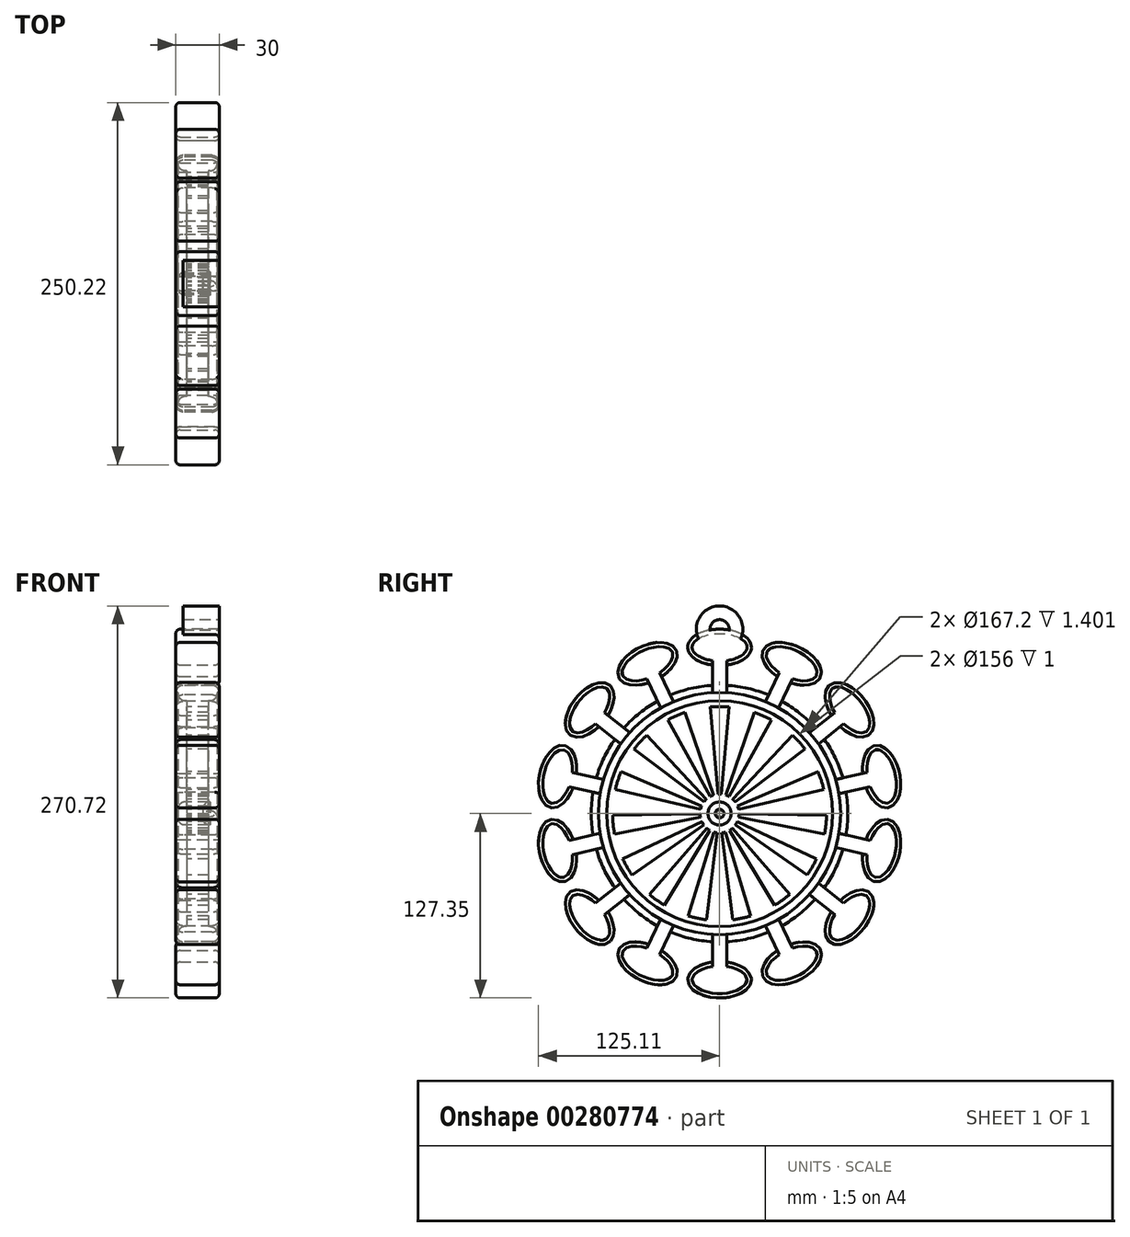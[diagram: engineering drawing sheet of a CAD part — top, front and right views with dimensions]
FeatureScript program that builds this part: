
annotation { "Feature Type Name" : "Feature", "Feature Type Description" : "" }
export const myFeature = defineFeature(function(context is Context, id is Id, definition is map)
    precondition{}
    {
        {
            var Q0;
            Q0=qCreatedBy(makeId("Front.planeOp"),FACE);
            var sketch = newSketch(context, id + "F0", { "sketchPlane" : qUnion([Q0])});
            skLineSegment(sketch, "E0", {"start": v(0, 0) * mm, "end": v(13.6, 0) * mm});
            skLineSegment(sketch, "E1", {"start": v(13.6, 0) * mm, "end": v(13.6, 8) * mm});
            skLineSegment(sketch, "E2", {"start": v(13.6, 8) * mm, "end": v(7.6, 8) * mm});
            skLineSegment(sketch, "E3", {"start": v(7.6, 8) * mm, "end": v(7.6, 78) * mm});
            skLineSegment(sketch, "E4", {"start": v(7.6, 78) * mm, "end": v(13.6, 78) * mm});
            skLineSegment(sketch, "E5", {"start": v(13.6, 78) * mm, "end": v(13.6, 83.6) * mm});
            skLineSegment(sketch, "E6", {"start": v(13.6, 83.6) * mm, "end": v(15, 83.6) * mm});
            skLineSegment(sketch, "E7", {"start": v(15, 83.6) * mm, "end": v(15, 88.64) * mm});
            skLineSegment(sketch, "E8", {"start": v(15, 88.64) * mm, "end": v(0, 88.64) * mm});
            skLineSegment(sketch, "E9.MirrorCS", {"start": v(0, 0) * mm, "end": v(-13.6, 0) * mm});
            skLineSegment(sketch, "E10.MirrorCS", {"start": v(-13.6, 0) * mm, "end": v(-13.6, 8) * mm});
            skLineSegment(sketch, "E11.MirrorCS", {"start": v(-13.6, 8) * mm, "end": v(-7.6, 8) * mm});
            skLineSegment(sketch, "E12.MirrorCS", {"start": v(-7.6, 8) * mm, "end": v(-7.6, 78) * mm});
            skLineSegment(sketch, "E13.MirrorCS", {"start": v(-7.6, 78) * mm, "end": v(-13.6, 78) * mm});
            skLineSegment(sketch, "E14.MirrorCS", {"start": v(-13.6, 78) * mm, "end": v(-13.6, 83.6) * mm});
            skLineSegment(sketch, "E15.MirrorCS", {"start": v(-13.6, 83.6) * mm, "end": v(-15, 83.6) * mm});
            skLineSegment(sketch, "E16.MirrorCS", {"start": v(-15, 83.6) * mm, "end": v(-15, 88.64) * mm});
            skLineSegment(sketch, "E17.MirrorCS", {"start": v(-15, 88.64) * mm, "end": v(0, 88.64) * mm});
            skSolve(sketch);
        }
        {
            var Q0;
            Q0 = qSketchRegion(id + "F0", true);
            var Q1;
            Q1=sQuery(id+"F0.wireOp",EDGE,"E0");
            revolve(context, id + "F1", {"entities" : qUnion([Q0]), "axis" : qUnion([Q1]), "revolveType" : RevolveType.FULL});
        }
        {
            var Q0;
            Q0=makeQuery(id+"F1.opRevolve","SWEPT_FACE",FACE,{"disambiguationData":[OSD([sQuery(id+"F0.wireOp",EDGE,"E12.MirrorCS")])]});
            var sketch = newSketch(context, id + "F2", { "sketchPlane" : qUnion([Q0])});
            skLineSegment(sketch, "E18", {"start": v(1.17, 13.39) * mm, "end": v(6.44, 73.6) * mm});
            skLineSegment(sketch, "E19", {"start": v(-1.17, 13.39) * mm, "end": v(-6.44, 73.6) * mm});
            skArc(sketch, "E20", {"start": v(1.17, 13.39) * mm, "mid": v(0, 13.44) * mm, "end": v(-1.17, 13.39) * mm});
            skArc(sketch, "E21", {"start": v(6.44, 73.6) * mm, "mid": v(0, 73.89) * mm, "end": v(-6.44, 73.6) * mm});
            skLineSegment(sketch, "E22.1.0", {"start": v(-4.37, 12.7) * mm, "end": v(-24.05, 69.86) * mm});
            skLineSegment(sketch, "E22.1.1", {"start": v(-6.51, 11.75) * mm, "end": v(-35.82, 64.62) * mm});
            skArc(sketch, "E22.1.2", {"start": v(-24.05, 69.86) * mm, "mid": v(-30.05, 67.5) * mm, "end": v(-35.82, 64.62) * mm});
            skArc(sketch, "E22.1.3", {"start": v(-4.37, 12.7) * mm, "mid": v(-5.47, 12.28) * mm, "end": v(-6.51, 11.75) * mm});
            skLineSegment(sketch, "E22.2.0", {"start": v(-9.16, 9.83) * mm, "end": v(-50.4, 54.04) * mm});
            skLineSegment(sketch, "E22.2.1", {"start": v(-10.73, 8.09) * mm, "end": v(-59, 44.47) * mm});
            skArc(sketch, "E22.2.2", {"start": v(-50.4, 54.04) * mm, "mid": v(-54.9, 49.44) * mm, "end": v(-59, 44.47) * mm});
            skArc(sketch, "E22.2.3", {"start": v(-9.16, 9.83) * mm, "mid": v(-9.99, 9) * mm, "end": v(-10.73, 8.09) * mm});
            skLineSegment(sketch, "E23.3.3.0", {"start": v(-13.1, 3.02) * mm, "end": v(-72, 16.62) * mm});
            skLineSegment(sketch, "E23.4.3.0", {"start": v(-12.37, 5.25) * mm, "end": v(-68.01, 28.87) * mm});
            skArc(sketch, "E23.6.3.0", {"start": v(-68.01, 28.87) * mm, "mid": v(-70.27, 22.83) * mm, "end": v(-72, 16.62) * mm});
            skArc(sketch, "E23.10.3.0", {"start": v(-12.37, 5.25) * mm, "mid": v(-12.78, 4.15) * mm, "end": v(-13.1, 3.02) * mm});
            skLineSegment(sketch, "E23.3.4.0", {"start": v(-13.2, -2.56) * mm, "end": v(-72.53, -14.1) * mm});
            skLineSegment(sketch, "E23.4.4.0", {"start": v(-13.43, -0.23) * mm, "end": v(-73.87, -1.29) * mm});
            skArc(sketch, "E23.6.4.0", {"start": v(-73.87, -1.29) * mm, "mid": v(-73.48, -7.72) * mm, "end": v(-72.53, -14.1) * mm});
            skArc(sketch, "E23.10.4.0", {"start": v(-13.43, -0.23) * mm, "mid": v(-13.36, -1.4) * mm, "end": v(-13.2, -2.56) * mm});
            skLineSegment(sketch, "E23.3.5.0", {"start": v(-11, -7.7) * mm, "end": v(-60.52, -42.38) * mm});
            skLineSegment(sketch, "E23.4.5.0", {"start": v(-12.18, -5.68) * mm, "end": v(-66.96, -31.23) * mm});
            skArc(sketch, "E23.6.5.0", {"start": v(-66.96, -31.23) * mm, "mid": v(-63.99, -36.94) * mm, "end": v(-60.52, -42.38) * mm});
            skArc(sketch, "E23.10.5.0", {"start": v(-12.18, -5.68) * mm, "mid": v(-11.64, -6.72) * mm, "end": v(-11, -7.7) * mm});
            skLineSegment(sketch, "E23.3.6.0", {"start": v(-6.92, -11.52) * mm, "end": v(-38.05, -63.33) * mm});
            skLineSegment(sketch, "E23.4.6.0", {"start": v(-8.82, -10.14) * mm, "end": v(-48.47, -55.76) * mm});
            skArc(sketch, "E23.6.6.0", {"start": v(-48.47, -55.76) * mm, "mid": v(-43.43, -59.78) * mm, "end": v(-38.05, -63.33) * mm});
            skArc(sketch, "E23.10.6.0", {"start": v(-8.82, -10.14) * mm, "mid": v(-7.9, -10.87) * mm, "end": v(-6.92, -11.52) * mm});
            skLineSegment(sketch, "E23.3.7.0", {"start": v(-1.64, -13.34) * mm, "end": v(-9, -73.34) * mm});
            skLineSegment(sketch, "E23.4.7.0", {"start": v(-3.93, -12.85) * mm, "end": v(-21.6, -70.66) * mm});
            skArc(sketch, "E23.6.7.0", {"start": v(-21.6, -70.66) * mm, "mid": v(-15.36, -72.27) * mm, "end": v(-9, -73.34) * mm});
            skArc(sketch, "E23.10.7.0", {"start": v(-3.93, -12.85) * mm, "mid": v(-2.8, -13.14) * mm, "end": v(-1.64, -13.34) * mm});
            skLineSegment(sketch, "E23.3.8.0", {"start": v(3.93, -12.85) * mm, "end": v(21.6, -70.66) * mm});
            skLineSegment(sketch, "E23.4.8.0", {"start": v(1.64, -13.34) * mm, "end": v(9, -73.34) * mm});
            skArc(sketch, "E23.6.8.0", {"start": v(9, -73.34) * mm, "mid": v(15.36, -72.27) * mm, "end": v(21.6, -70.66) * mm});
            skArc(sketch, "E23.10.8.0", {"start": v(1.64, -13.34) * mm, "mid": v(2.8, -13.14) * mm, "end": v(3.93, -12.85) * mm});
            skLineSegment(sketch, "E23.3.9.0", {"start": v(8.82, -10.14) * mm, "end": v(48.47, -55.76) * mm});
            skLineSegment(sketch, "E23.4.9.0", {"start": v(6.92, -11.52) * mm, "end": v(38.05, -63.33) * mm});
            skArc(sketch, "E23.6.9.0", {"start": v(38.05, -63.33) * mm, "mid": v(43.43, -59.78) * mm, "end": v(48.47, -55.76) * mm});
            skArc(sketch, "E23.10.9.0", {"start": v(6.92, -11.52) * mm, "mid": v(7.9, -10.87) * mm, "end": v(8.82, -10.14) * mm});
            skLineSegment(sketch, "E23.3.10.0", {"start": v(12.18, -5.68) * mm, "end": v(66.96, -31.23) * mm});
            skLineSegment(sketch, "E23.4.10.0", {"start": v(11, -7.7) * mm, "end": v(60.52, -42.38) * mm});
            skArc(sketch, "E23.6.10.0", {"start": v(60.52, -42.38) * mm, "mid": v(63.99, -36.94) * mm, "end": v(66.96, -31.23) * mm});
            skArc(sketch, "E23.10.10.0", {"start": v(11, -7.7) * mm, "mid": v(11.64, -6.72) * mm, "end": v(12.18, -5.68) * mm});
            skLineSegment(sketch, "E23.3.11.0", {"start": v(13.43, -0.23) * mm, "end": v(73.87, -1.29) * mm});
            skLineSegment(sketch, "E23.4.11.0", {"start": v(13.2, -2.56) * mm, "end": v(72.53, -14.1) * mm});
            skArc(sketch, "E23.6.11.0", {"start": v(72.53, -14.1) * mm, "mid": v(73.48, -7.72) * mm, "end": v(73.87, -1.29) * mm});
            skArc(sketch, "E23.10.11.0", {"start": v(13.2, -2.56) * mm, "mid": v(13.36, -1.4) * mm, "end": v(13.43, -0.23) * mm});
            skLineSegment(sketch, "E23.3.12.0", {"start": v(12.37, 5.25) * mm, "end": v(68.01, 28.87) * mm});
            skLineSegment(sketch, "E23.4.12.0", {"start": v(13.1, 3.02) * mm, "end": v(72, 16.62) * mm});
            skArc(sketch, "E23.6.12.0", {"start": v(72, 16.62) * mm, "mid": v(70.27, 22.83) * mm, "end": v(68.01, 28.87) * mm});
            skArc(sketch, "E23.10.12.0", {"start": v(13.1, 3.02) * mm, "mid": v(12.78, 4.15) * mm, "end": v(12.37, 5.25) * mm});
            skLineSegment(sketch, "E23.3.13.0", {"start": v(9.16, 9.83) * mm, "end": v(50.4, 54.04) * mm});
            skLineSegment(sketch, "E23.4.13.0", {"start": v(10.73, 8.09) * mm, "end": v(59, 44.47) * mm});
            skArc(sketch, "E23.6.13.0", {"start": v(59, 44.47) * mm, "mid": v(54.9, 49.44) * mm, "end": v(50.4, 54.04) * mm});
            skArc(sketch, "E23.10.13.0", {"start": v(10.73, 8.09) * mm, "mid": v(9.99, 9) * mm, "end": v(9.16, 9.83) * mm});
            skLineSegment(sketch, "E23.3.14.0", {"start": v(4.37, 12.7) * mm, "end": v(24.05, 69.86) * mm});
            skLineSegment(sketch, "E23.4.14.0", {"start": v(6.51, 11.75) * mm, "end": v(35.82, 64.62) * mm});
            skArc(sketch, "E23.6.14.0", {"start": v(35.82, 64.62) * mm, "mid": v(30.05, 67.5) * mm, "end": v(24.05, 69.86) * mm});
            skArc(sketch, "E23.10.14.0", {"start": v(6.51, 11.75) * mm, "mid": v(5.47, 12.28) * mm, "end": v(4.37, 12.7) * mm});
            skSolve(sketch);
        }
        {
            var Q0;
            Q0 = qSketchRegion(id + "F2", true);
            extrude(context, id + "F3", {"entities" : qUnion([Q0]), "operationType" : NewBodyOperationType.REMOVE, "oppositeDirection" : true, "depth" : 25 * mm});
        }
        {
            var Q0;
            Q0=makeQuery(id+"F1.opRevolve","SWEPT_FACE",FACE,{"disambiguationData":[OSD([sQuery(id+"F0.wireOp",EDGE,"E7")])]});
            var sketch = newSketch(context, id + "F4", { "sketchPlane" : qUnion([Q0])});
            skEllipticalArc(sketch, "E24", {});
            skLineSegment(sketch, "E25.0", {"start": v(5, 85) * mm, "end": v(5, 102.6) * mm});
            skLineSegment(sketch, "E26.0", {"start": v(-5, 85) * mm, "end": v(-5, 102.6) * mm});
            skPoint(sketch, "E27.startSnap0", {"position": v(-5, 85) * mm});
            skPoint(sketch, "E27.endSnap0", {"position": v(5, 85) * mm});
            skPoint(sketch, "E28.orphan", {"position": v(-5, 114.8) * mm});
            skPoint(sketch, "E29.orphan", {"position": v(5, 114.8) * mm});
            skPoint(sketch, "E30.orphan", {"position": v(-7.8, 85) * mm});
            skPoint(sketch, "E31.orphan", {"position": v(-5, 55.18) * mm});
            skPoint(sketch, "E32.orphan", {"position": v(5, 55.18) * mm});
            skPoint(sketch, "E33.orphan", {"position": v(7.79, 85) * mm});
            skLineSegment(sketch, "E34", {"start": v(-5, 85) * mm, "end": v(5, 85) * mm});
            skEllipticalArc(sketch, "E35.1.0", {});
            skLineSegment(sketch, "E35.1.1", {"start": v(-41.38, 74.4) * mm, "end": v(-32.37, 78.75) * mm});
            skLineSegment(sketch, "E35.1.2", {"start": v(-41.38, 74.4) * mm, "end": v(-49.02, 90.26) * mm});
            skLineSegment(sketch, "E35.1.3", {"start": v(-32.37, 78.75) * mm, "end": v(-40, 94.6) * mm});
            skEllipticalArc(sketch, "E35.2.0", {});
            skLineSegment(sketch, "E35.2.1", {"start": v(-69.57, 49.08) * mm, "end": v(-63.33, 56.9) * mm});
            skLineSegment(sketch, "E35.2.2", {"start": v(-69.57, 49.08) * mm, "end": v(-83.33, 60.05) * mm});
            skLineSegment(sketch, "E35.2.3", {"start": v(-63.33, 56.9) * mm, "end": v(-77.1, 67.87) * mm});
            skPoint(sketch, "E35.center", {"position": v(0, 0) * mm});
            skLineSegment(sketch, "E36.4.3.0", {"start": v(-83.98, 14.04) * mm, "end": v(-81.75, 23.79) * mm});
            skEllipticalArc(sketch, "E36.5.3.0", {});
            skLineSegment(sketch, "E36.7.3.0", {"start": v(-83.98, 14.04) * mm, "end": v(-101.13, 17.95) * mm});
            skLineSegment(sketch, "E36.10.3.0", {"start": v(-81.75, 23.79) * mm, "end": v(-98.9, 27.7) * mm});
            skLineSegment(sketch, "E36.4.4.0", {"start": v(-81.75, -23.79) * mm, "end": v(-83.98, -14.04) * mm});
            skEllipticalArc(sketch, "E36.5.4.0", {});
            skLineSegment(sketch, "E36.7.4.0", {"start": v(-81.75, -23.79) * mm, "end": v(-98.9, -27.7) * mm});
            skLineSegment(sketch, "E36.10.4.0", {"start": v(-83.98, -14.04) * mm, "end": v(-101.13, -17.95) * mm});
            skLineSegment(sketch, "E36.4.5.0", {"start": v(-63.33, -56.9) * mm, "end": v(-69.57, -49.08) * mm});
            skEllipticalArc(sketch, "E36.5.5.0", {});
            skLineSegment(sketch, "E36.7.5.0", {"start": v(-63.33, -56.9) * mm, "end": v(-77.1, -67.87) * mm});
            skLineSegment(sketch, "E36.10.5.0", {"start": v(-69.57, -49.08) * mm, "end": v(-83.33, -60.05) * mm});
            skLineSegment(sketch, "E36.4.6.0", {"start": v(-32.37, -78.75) * mm, "end": v(-41.38, -74.4) * mm});
            skEllipticalArc(sketch, "E36.5.6.0", {});
            skLineSegment(sketch, "E36.7.6.0", {"start": v(-32.37, -78.75) * mm, "end": v(-40, -94.6) * mm});
            skLineSegment(sketch, "E36.10.6.0", {"start": v(-41.38, -74.4) * mm, "end": v(-49.02, -90.26) * mm});
            skLineSegment(sketch, "E36.4.7.0", {"start": v(5, -85) * mm, "end": v(-5, -85) * mm});
            skEllipticalArc(sketch, "E36.5.7.0", {});
            skLineSegment(sketch, "E36.7.7.0", {"start": v(5, -85) * mm, "end": v(5, -102.6) * mm});
            skLineSegment(sketch, "E36.10.7.0", {"start": v(-5, -85) * mm, "end": v(-5, -102.6) * mm});
            skLineSegment(sketch, "E36.4.8.0", {"start": v(41.38, -74.4) * mm, "end": v(32.37, -78.75) * mm});
            skEllipticalArc(sketch, "E36.5.8.0", {});
            skLineSegment(sketch, "E36.7.8.0", {"start": v(41.38, -74.4) * mm, "end": v(49.02, -90.26) * mm});
            skLineSegment(sketch, "E36.10.8.0", {"start": v(32.37, -78.75) * mm, "end": v(40, -94.6) * mm});
            skLineSegment(sketch, "E36.4.9.0", {"start": v(69.57, -49.08) * mm, "end": v(63.33, -56.9) * mm});
            skEllipticalArc(sketch, "E36.5.9.0", {});
            skLineSegment(sketch, "E36.7.9.0", {"start": v(69.57, -49.08) * mm, "end": v(83.33, -60.05) * mm});
            skLineSegment(sketch, "E36.10.9.0", {"start": v(63.33, -56.9) * mm, "end": v(77.1, -67.87) * mm});
            skLineSegment(sketch, "E36.4.10.0", {"start": v(83.98, -14.04) * mm, "end": v(81.75, -23.79) * mm});
            skEllipticalArc(sketch, "E36.5.10.0", {});
            skLineSegment(sketch, "E36.7.10.0", {"start": v(83.98, -14.04) * mm, "end": v(101.13, -17.95) * mm});
            skLineSegment(sketch, "E36.10.10.0", {"start": v(81.75, -23.79) * mm, "end": v(98.9, -27.7) * mm});
            skLineSegment(sketch, "E36.4.11.0", {"start": v(81.75, 23.79) * mm, "end": v(83.98, 14.04) * mm});
            skEllipticalArc(sketch, "E36.5.11.0", {});
            skLineSegment(sketch, "E36.7.11.0", {"start": v(81.75, 23.79) * mm, "end": v(98.9, 27.7) * mm});
            skLineSegment(sketch, "E36.10.11.0", {"start": v(83.98, 14.04) * mm, "end": v(101.13, 17.95) * mm});
            skLineSegment(sketch, "E36.4.12.0", {"start": v(63.33, 56.9) * mm, "end": v(69.57, 49.08) * mm});
            skEllipticalArc(sketch, "E36.5.12.0", {});
            skLineSegment(sketch, "E36.7.12.0", {"start": v(63.33, 56.9) * mm, "end": v(77.1, 67.87) * mm});
            skLineSegment(sketch, "E36.10.12.0", {"start": v(69.57, 49.08) * mm, "end": v(83.33, 60.05) * mm});
            skLineSegment(sketch, "E36.4.13.0", {"start": v(32.37, 78.75) * mm, "end": v(41.38, 74.4) * mm});
            skEllipticalArc(sketch, "E36.5.13.0", {});
            skLineSegment(sketch, "E36.7.13.0", {"start": v(32.37, 78.75) * mm, "end": v(40, 94.6) * mm});
            skLineSegment(sketch, "E36.10.13.0", {"start": v(41.38, 74.4) * mm, "end": v(49.02, 90.26) * mm});
            const initialGuessF4  = {"E24": [0, 0.11480870097875595, 1, 0, 0.0220187958329916, 0.012546207894898827, 4.941465968806927, 4.483311991962452], "E35.1.0": [-0.049813628463892284, 0.10343906534617711, 0.9009688679024191, 0.4338837391175582, 0.0220187958329916, 0.012546207894898827, 4.941465968806927, 4.483311991962452], "E35.2.0": [-0.08976105688644952, 0.07158205422490314, 0.6234898018587336, 0.7818314824680298, 0.0220187958329916, 0.012546207894898827, 4.941465968806927, 4.483311991962452], "E36.5.3.0": [-0.11193020714552583, 0.025547339368104008, 0.22252093395631445, 0.9749279121818236, 0.0220187958329916, 0.012546207894898827, 4.941465968806927, 4.483311991962452], "E36.5.4.0": [-0.11193020714552583, -0.025547339368103994, -0.22252093395631434, 0.9749279121818236, 0.0220187958329916, 0.012546207894898827, 4.941465968806927, 4.483311991962452], "E36.5.5.0": [-0.08976105688644952, -0.07158205422490313, -0.6234898018587335, 0.7818314824680299, 0.0220187958329916, 0.012546207894898827, 4.941465968806927, 4.483311991962452], "E36.5.6.0": [-0.0498136284638923, -0.1034390653461771, -0.900968867902419, 0.43388373911755823, 0.0220187958329916, 0.012546207894898827, 4.941465968806927, 4.483311991962451], "E36.5.7.0": [0, -0.11480870097875595, -1, 0, 0.0220187958329916, 0.012546207894898827, 4.941465968806927, 4.483311991962452], "E36.5.8.0": [0.04981362846389227, -0.10343906534617711, -0.9009688679024191, -0.433883739117558, 0.0220187958329916, 0.012546207894898827, 4.941465968806926, 4.483311991962451], "E36.5.9.0": [0.0897610568864495, -0.07158205422490316, -0.6234898018587337, -0.7818314824680297, 0.0220187958329916, 0.012546207894898827, 4.941465968806927, 4.483311991962452], "E36.5.10.0": [0.11193020714552583, -0.02554733936810402, -0.2225209339563146, -0.9749279121818236, 0.0220187958329916, 0.012546207894898827, 4.941465968806927, 4.483311991962452], "E36.5.11.0": [0.11193020714552586, 0.02554733936810388, 0.22252093395631334, -0.9749279121818238, 0.0220187958329916, 0.012546207894898827, 4.941465968806927, 4.483311991962452], "E36.5.12.0": [0.08976105688644952, 0.07158205422490312, 0.6234898018587334, -0.7818314824680299, 0.0220187958329916, 0.012546207894898827, 4.941465968806927, 4.483311991962452], "E36.5.13.0": [0.049813628463892215, 0.10343906534617714, 0.9009688679024194, -0.4338837391175575, 0.0220187958329916, 0.012546207894898827, 4.941465968806927, 4.483311991962452]};
            skSetInitialGuess(sketch, initialGuessF4);
            skSolve(sketch);
        }
        {
            var Q0;
            Q0 = qSketchRegion(id + "F4", true);
            extrude(context, id + "F5", {"entities" : qUnion([Q0]), "operationType" : NewBodyOperationType.ADD, "oppositeDirection" : true, "depth" : 30 * mm});
        }
        {
            var Q0;
            Q0=makeQuery(id+"F5.boolean.opBoolean","MERGE",FACE,{"derivedFrom":[makeQuery(id+"F1.opRevolve","SWEPT_FACE",FACE,{"disambiguationData":[OSD([sQuery(id+"F0.wireOp",EDGE,"E7")])]}),makeQuery(id+"F5.opExtrude","CAP_FACE",FACE,{"disambiguationData":[OSD([sQuery(id+"F4.wireOp",EDGE,"E24"),sQuery(id+"F4.wireOp",EDGE,"E25.0"),sQuery(id+"F4.wireOp",EDGE,"E26.0"),sQuery(id+"F4.wireOp",EDGE,"E34")])],"isStart":true}),makeQuery(id+"F5.opExtrude","CAP_FACE",FACE,{"disambiguationData":[OSD([sQuery(id+"F4.wireOp",EDGE,"E35.1.0"),sQuery(id+"F4.wireOp",EDGE,"E35.1.1"),sQuery(id+"F4.wireOp",EDGE,"E35.1.2"),sQuery(id+"F4.wireOp",EDGE,"E35.1.3")])],"isStart":true}),makeQuery(id+"F5.opExtrude","CAP_FACE",FACE,{"disambiguationData":[OSD([sQuery(id+"F4.wireOp",EDGE,"E35.2.0"),sQuery(id+"F4.wireOp",EDGE,"E35.2.1"),sQuery(id+"F4.wireOp",EDGE,"E35.2.2"),sQuery(id+"F4.wireOp",EDGE,"E35.2.3")])],"isStart":true}),makeQuery(id+"F5.opExtrude","CAP_FACE",FACE,{"disambiguationData":[OSD([sQuery(id+"F4.wireOp",EDGE,"E36.4.3.0"),sQuery(id+"F4.wireOp",EDGE,"E36.5.3.0"),sQuery(id+"F4.wireOp",EDGE,"E36.7.3.0"),sQuery(id+"F4.wireOp",EDGE,"E36.10.3.0")])],"isStart":true}),makeQuery(id+"F5.opExtrude","CAP_FACE",FACE,{"disambiguationData":[OSD([sQuery(id+"F4.wireOp",EDGE,"E36.4.4.0"),sQuery(id+"F4.wireOp",EDGE,"E36.5.4.0"),sQuery(id+"F4.wireOp",EDGE,"E36.7.4.0"),sQuery(id+"F4.wireOp",EDGE,"E36.10.4.0")])],"isStart":true}),makeQuery(id+"F5.opExtrude","CAP_FACE",FACE,{"disambiguationData":[OSD([sQuery(id+"F4.wireOp",EDGE,"E36.4.5.0"),sQuery(id+"F4.wireOp",EDGE,"E36.5.5.0"),sQuery(id+"F4.wireOp",EDGE,"E36.7.5.0"),sQuery(id+"F4.wireOp",EDGE,"E36.10.5.0")])],"isStart":true}),makeQuery(id+"F5.opExtrude","CAP_FACE",FACE,{"disambiguationData":[OSD([sQuery(id+"F4.wireOp",EDGE,"E36.4.6.0"),sQuery(id+"F4.wireOp",EDGE,"E36.5.6.0"),sQuery(id+"F4.wireOp",EDGE,"E36.7.6.0"),sQuery(id+"F4.wireOp",EDGE,"E36.10.6.0")])],"isStart":true}),makeQuery(id+"F5.opExtrude","CAP_FACE",FACE,{"disambiguationData":[OSD([sQuery(id+"F4.wireOp",EDGE,"E36.4.7.0"),sQuery(id+"F4.wireOp",EDGE,"E36.5.7.0"),sQuery(id+"F4.wireOp",EDGE,"E36.7.7.0"),sQuery(id+"F4.wireOp",EDGE,"E36.10.7.0")])],"isStart":true}),makeQuery(id+"F5.opExtrude","CAP_FACE",FACE,{"disambiguationData":[OSD([sQuery(id+"F4.wireOp",EDGE,"E36.4.8.0"),sQuery(id+"F4.wireOp",EDGE,"E36.5.8.0"),sQuery(id+"F4.wireOp",EDGE,"E36.7.8.0"),sQuery(id+"F4.wireOp",EDGE,"E36.10.8.0")])],"isStart":true}),makeQuery(id+"F5.opExtrude","CAP_FACE",FACE,{"disambiguationData":[OSD([sQuery(id+"F4.wireOp",EDGE,"E36.4.9.0"),sQuery(id+"F4.wireOp",EDGE,"E36.5.9.0"),sQuery(id+"F4.wireOp",EDGE,"E36.7.9.0"),sQuery(id+"F4.wireOp",EDGE,"E36.10.9.0")])],"isStart":true}),makeQuery(id+"F5.opExtrude","CAP_FACE",FACE,{"disambiguationData":[OSD([sQuery(id+"F4.wireOp",EDGE,"E36.4.10.0"),sQuery(id+"F4.wireOp",EDGE,"E36.5.10.0"),sQuery(id+"F4.wireOp",EDGE,"E36.7.10.0"),sQuery(id+"F4.wireOp",EDGE,"E36.10.10.0")])],"isStart":true}),makeQuery(id+"F5.opExtrude","CAP_FACE",FACE,{"disambiguationData":[OSD([sQuery(id+"F4.wireOp",EDGE,"E36.4.11.0"),sQuery(id+"F4.wireOp",EDGE,"E36.5.11.0"),sQuery(id+"F4.wireOp",EDGE,"E36.7.11.0"),sQuery(id+"F4.wireOp",EDGE,"E36.10.11.0")])],"isStart":true}),makeQuery(id+"F5.opExtrude","CAP_FACE",FACE,{"disambiguationData":[OSD([sQuery(id+"F4.wireOp",EDGE,"E36.4.12.0"),sQuery(id+"F4.wireOp",EDGE,"E36.5.12.0"),sQuery(id+"F4.wireOp",EDGE,"E36.7.12.0"),sQuery(id+"F4.wireOp",EDGE,"E36.10.12.0")])],"isStart":true}),makeQuery(id+"F5.opExtrude","CAP_FACE",FACE,{"disambiguationData":[OSD([sQuery(id+"F4.wireOp",EDGE,"E36.4.13.0"),sQuery(id+"F4.wireOp",EDGE,"E36.5.13.0"),sQuery(id+"F4.wireOp",EDGE,"E36.7.13.0"),sQuery(id+"F4.wireOp",EDGE,"E36.10.13.0")])],"isStart":true})]});
            var sketch = newSketch(context, id + "F6", { "sketchPlane" : qUnion([Q0])});
            skArc(sketch, "E37", {"start": v(15.58, 123.67) * mm, "mid": v(0, 143.37) * mm, "end": v(-15.58, 123.67) * mm});
            skArc(sketch, "E38", {"start": v(6.55, 126.94) * mm, "mid": v(0, 133.92) * mm, "end": v(-6.55, 126.94) * mm});
            skPoint(sketch, "E39.center.orphan", {"position": v(0, 111.34) * mm});
            skLineSegment(sketch, "E40", {"start": v(-15.58, 123.67) * mm, "end": v(-6.55, 126.94) * mm});
            skLineSegment(sketch, "E41", {"start": v(6.55, 126.94) * mm, "end": v(15.58, 123.67) * mm});
            skSolve(sketch);
        }
        {
            var Q0;
            Q0 = qSketchRegion(id + "F6", true);
            extrude(context, id + "F7", {"entities" : qUnion([Q0]), "operationType" : NewBodyOperationType.ADD, "oppositeDirection" : true, "depth" : 25 * mm});
        }
        {
            var Q0;
            {var subQ1=sQuery(id+"F0.wireOp",EDGE,"E8");var subQ2=sQuery(id+"F4.wireOp",EDGE,"E35.1.2");var subQ3=sQuery(id+"F0.wireOp",EDGE,"E7");Q0=makeQuery(id+"F5.boolean.opBoolean","SPLIT",EDGE,{"disambiguationData":[TD([makeQuery(id+"F5.opExtrude","SWEPT_FACE",FACE,{"disambiguationData":[OSD([subQ2])]})])],"derivedFrom":makeQuery(id+"F1.opRevolve","SWEPT_EDGE",EDGE,{"disambiguationData":[OSD([subQ3,subQ1])]})});}
            var Q1;
            {var subQ1=sQuery(id+"F4.wireOp",EDGE,"E35.2.2");var subQ2=sQuery(id+"F0.wireOp",EDGE,"E8");var subQ3=sQuery(id+"F0.wireOp",EDGE,"E7");Q1=makeQuery(id+"F5.boolean.opBoolean","SPLIT",EDGE,{"disambiguationData":[TD([makeQuery(id+"F5.opExtrude","SWEPT_FACE",FACE,{"disambiguationData":[OSD([subQ1])]})])],"derivedFrom":makeQuery(id+"F1.opRevolve","SWEPT_EDGE",EDGE,{"disambiguationData":[OSD([subQ3,subQ2])]})});}
            var Q2;
            {var subQ1=sQuery(id+"F4.wireOp",EDGE,"E36.7.3.0");var subQ2=sQuery(id+"F0.wireOp",EDGE,"E8");var subQ3=sQuery(id+"F0.wireOp",EDGE,"E7");Q2=makeQuery(id+"F5.boolean.opBoolean","SPLIT",EDGE,{"disambiguationData":[TD([makeQuery(id+"F5.opExtrude","SWEPT_FACE",FACE,{"disambiguationData":[OSD([subQ1])]})])],"derivedFrom":makeQuery(id+"F1.opRevolve","SWEPT_EDGE",EDGE,{"disambiguationData":[OSD([subQ3,subQ2])]})});}
            var Q3;
            {var subQ1=sQuery(id+"F4.wireOp",EDGE,"E36.7.4.0");var subQ2=sQuery(id+"F0.wireOp",EDGE,"E7");var subQ3=sQuery(id+"F0.wireOp",EDGE,"E8");Q3=makeQuery(id+"F5.boolean.opBoolean","SPLIT",EDGE,{"disambiguationData":[TD([makeQuery(id+"F5.opExtrude","SWEPT_FACE",FACE,{"disambiguationData":[OSD([subQ1])]})])],"derivedFrom":makeQuery(id+"F1.opRevolve","SWEPT_EDGE",EDGE,{"disambiguationData":[OSD([subQ2,subQ3])]})});}
            var Q4;
            {var subQ0=sQuery(id+"F0.wireOp",EDGE,"E8");var subQ2=sQuery(id+"F0.wireOp",EDGE,"E7");var subQ3=sQuery(id+"F4.wireOp",EDGE,"E26.0");Q4=makeQuery(id+"F5.boolean.opBoolean","SPLIT",EDGE,{"disambiguationData":[TD([makeQuery(id+"F5.opExtrude","SWEPT_FACE",FACE,{"disambiguationData":[OSD([subQ3])]})])],"derivedFrom":makeQuery(id+"F1.opRevolve","SWEPT_EDGE",EDGE,{"disambiguationData":[OSD([subQ2,subQ0])]})});}
            var Q5;
            {var subQ0=sQuery(id+"F0.wireOp",EDGE,"E8");var subQ2=sQuery(id+"F0.wireOp",EDGE,"E7");var subQ3=sQuery(id+"F4.wireOp",EDGE,"E25.0");Q5=makeQuery(id+"F5.boolean.opBoolean","SPLIT",EDGE,{"disambiguationData":[TD([makeQuery(id+"F5.opExtrude","SWEPT_FACE",FACE,{"disambiguationData":[OSD([subQ3])]})])],"derivedFrom":makeQuery(id+"F1.opRevolve","SWEPT_EDGE",EDGE,{"disambiguationData":[OSD([subQ2,subQ0])]})});}
            var Q6;
            {var subQ1=sQuery(id+"F0.wireOp",EDGE,"E8");var subQ2=sQuery(id+"F0.wireOp",EDGE,"E7");var subQ3=sQuery(id+"F4.wireOp",EDGE,"E36.7.12.0");Q6=makeQuery(id+"F5.boolean.opBoolean","SPLIT",EDGE,{"disambiguationData":[TD([makeQuery(id+"F5.opExtrude","SWEPT_FACE",FACE,{"disambiguationData":[OSD([subQ3])]})])],"derivedFrom":makeQuery(id+"F1.opRevolve","SWEPT_EDGE",EDGE,{"disambiguationData":[OSD([subQ2,subQ1])]})});}
            var Q7;
            {var subQ1=sQuery(id+"F0.wireOp",EDGE,"E8");var subQ2=sQuery(id+"F0.wireOp",EDGE,"E7");var subQ3=sQuery(id+"F4.wireOp",EDGE,"E36.7.11.0");Q7=makeQuery(id+"F5.boolean.opBoolean","SPLIT",EDGE,{"disambiguationData":[TD([makeQuery(id+"F5.opExtrude","SWEPT_FACE",FACE,{"disambiguationData":[OSD([subQ3])]})])],"derivedFrom":makeQuery(id+"F1.opRevolve","SWEPT_EDGE",EDGE,{"disambiguationData":[OSD([subQ2,subQ1])]})});}
            var Q8;
            {var subQ1=sQuery(id+"F0.wireOp",EDGE,"E8");var subQ2=sQuery(id+"F0.wireOp",EDGE,"E7");var subQ3=sQuery(id+"F4.wireOp",EDGE,"E36.7.10.0");Q8=makeQuery(id+"F5.boolean.opBoolean","SPLIT",EDGE,{"disambiguationData":[TD([makeQuery(id+"F5.opExtrude","SWEPT_FACE",FACE,{"disambiguationData":[OSD([subQ3])]})])],"derivedFrom":makeQuery(id+"F1.opRevolve","SWEPT_EDGE",EDGE,{"disambiguationData":[OSD([subQ2,subQ1])]})});}
            var Q9;
            {var subQ1=sQuery(id+"F0.wireOp",EDGE,"E8");var subQ2=sQuery(id+"F0.wireOp",EDGE,"E7");var subQ3=sQuery(id+"F4.wireOp",EDGE,"E36.7.9.0");Q9=makeQuery(id+"F5.boolean.opBoolean","SPLIT",EDGE,{"disambiguationData":[TD([makeQuery(id+"F5.opExtrude","SWEPT_FACE",FACE,{"disambiguationData":[OSD([subQ3])]})])],"derivedFrom":makeQuery(id+"F1.opRevolve","SWEPT_EDGE",EDGE,{"disambiguationData":[OSD([subQ2,subQ1])]})});}
            var Q10;
            {var subQ0=sQuery(id+"F0.wireOp",EDGE,"E8");var subQ2=sQuery(id+"F0.wireOp",EDGE,"E7");var subQ3=sQuery(id+"F4.wireOp",EDGE,"E36.7.8.0");Q10=makeQuery(id+"F5.boolean.opBoolean","SPLIT",EDGE,{"disambiguationData":[TD([makeQuery(id+"F5.opExtrude","SWEPT_FACE",FACE,{"disambiguationData":[OSD([subQ3])]})])],"derivedFrom":makeQuery(id+"F1.opRevolve","SWEPT_EDGE",EDGE,{"disambiguationData":[OSD([subQ2,subQ0])]})});}
            var Q11;
            {var subQ0=sQuery(id+"F4.wireOp",EDGE,"E36.7.7.0");var subQ1=sQuery(id+"F0.wireOp",EDGE,"E8");var subQ2=sQuery(id+"F0.wireOp",EDGE,"E7");Q11=makeQuery(id+"F5.boolean.opBoolean","SPLIT",EDGE,{"disambiguationData":[TD([makeQuery(id+"F5.opExtrude","SWEPT_FACE",FACE,{"disambiguationData":[OSD([subQ0])]})])],"derivedFrom":makeQuery(id+"F1.opRevolve","SWEPT_EDGE",EDGE,{"disambiguationData":[OSD([subQ2,subQ1])]})});}
            var Q12;
            {var subQ0=sQuery(id+"F4.wireOp",EDGE,"E36.7.6.0");var subQ1=sQuery(id+"F0.wireOp",EDGE,"E8");var subQ2=sQuery(id+"F0.wireOp",EDGE,"E7");Q12=makeQuery(id+"F5.boolean.opBoolean","SPLIT",EDGE,{"disambiguationData":[TD([makeQuery(id+"F5.opExtrude","SWEPT_FACE",FACE,{"disambiguationData":[OSD([subQ0])]})])],"derivedFrom":makeQuery(id+"F1.opRevolve","SWEPT_EDGE",EDGE,{"disambiguationData":[OSD([subQ2,subQ1])]})});}
            var Q13;
            {var subQ1=sQuery(id+"F4.wireOp",EDGE,"E36.7.5.0");var subQ2=sQuery(id+"F0.wireOp",EDGE,"E8");var subQ3=sQuery(id+"F0.wireOp",EDGE,"E7");Q13=makeQuery(id+"F5.boolean.opBoolean","SPLIT",EDGE,{"disambiguationData":[TD([makeQuery(id+"F5.opExtrude","SWEPT_FACE",FACE,{"disambiguationData":[OSD([subQ1])]})])],"derivedFrom":makeQuery(id+"F1.opRevolve","SWEPT_EDGE",EDGE,{"disambiguationData":[OSD([subQ3,subQ2])]})});}
            fillet(context, id + "F8", {"entities" : qUnion([Q0, Q1, Q2, Q3, Q4, Q5, Q6, Q7, Q8, Q9, Q10, Q11, Q12, Q13]), "radius" : 5 * mm, "tangentPropagation" : true, "allowEdgeOverflow" : false});
        }
        {
            var Q0;
            {var subQ0=sQuery(id+"F0.wireOp",EDGE,"E16.MirrorCS");var subQ1=sQuery(id+"F0.wireOp",EDGE,"E17.MirrorCS");var subQ2=sQuery(id+"F4.wireOp",EDGE,"E36.7.9.0");Q0=makeQuery(id+"F5.boolean.opBoolean","SPLIT",EDGE,{"disambiguationData":[TD([makeQuery(id+"F5.opExtrude","SWEPT_FACE",FACE,{"disambiguationData":[OSD([subQ2])]})])],"derivedFrom":makeQuery(id+"F1.opRevolve","SWEPT_EDGE",EDGE,{"disambiguationData":[OSD([subQ0,subQ1])]})});}
            var Q1;
            {var subQ0=sQuery(id+"F0.wireOp",EDGE,"E16.MirrorCS");var subQ1=sQuery(id+"F0.wireOp",EDGE,"E17.MirrorCS");var subQ3=sQuery(id+"F4.wireOp",EDGE,"E36.7.8.0");Q1=makeQuery(id+"F5.boolean.opBoolean","SPLIT",EDGE,{"disambiguationData":[TD([makeQuery(id+"F5.opExtrude","SWEPT_FACE",FACE,{"disambiguationData":[OSD([subQ3])]})])],"derivedFrom":makeQuery(id+"F1.opRevolve","SWEPT_EDGE",EDGE,{"disambiguationData":[OSD([subQ0,subQ1])]})});}
            var Q2;
            {var subQ0=sQuery(id+"F4.wireOp",EDGE,"E36.7.7.0");var subQ1=sQuery(id+"F0.wireOp",EDGE,"E16.MirrorCS");var subQ2=sQuery(id+"F0.wireOp",EDGE,"E17.MirrorCS");Q2=makeQuery(id+"F5.boolean.opBoolean","SPLIT",EDGE,{"disambiguationData":[TD([makeQuery(id+"F5.opExtrude","SWEPT_FACE",FACE,{"disambiguationData":[OSD([subQ0])]})])],"derivedFrom":makeQuery(id+"F1.opRevolve","SWEPT_EDGE",EDGE,{"disambiguationData":[OSD([subQ1,subQ2])]})});}
            var Q3;
            {var subQ0=sQuery(id+"F4.wireOp",EDGE,"E36.7.6.0");var subQ1=sQuery(id+"F0.wireOp",EDGE,"E16.MirrorCS");var subQ2=sQuery(id+"F0.wireOp",EDGE,"E17.MirrorCS");Q3=makeQuery(id+"F5.boolean.opBoolean","SPLIT",EDGE,{"disambiguationData":[TD([makeQuery(id+"F5.opExtrude","SWEPT_FACE",FACE,{"disambiguationData":[OSD([subQ0])]})])],"derivedFrom":makeQuery(id+"F1.opRevolve","SWEPT_EDGE",EDGE,{"disambiguationData":[OSD([subQ1,subQ2])]})});}
            var Q4;
            {var subQ1=sQuery(id+"F4.wireOp",EDGE,"E36.7.5.0");var subQ2=sQuery(id+"F0.wireOp",EDGE,"E16.MirrorCS");var subQ3=sQuery(id+"F0.wireOp",EDGE,"E17.MirrorCS");Q4=makeQuery(id+"F5.boolean.opBoolean","SPLIT",EDGE,{"disambiguationData":[TD([makeQuery(id+"F5.opExtrude","SWEPT_FACE",FACE,{"disambiguationData":[OSD([subQ1])]})])],"derivedFrom":makeQuery(id+"F1.opRevolve","SWEPT_EDGE",EDGE,{"disambiguationData":[OSD([subQ2,subQ3])]})});}
            var Q5;
            {var subQ1=sQuery(id+"F4.wireOp",EDGE,"E36.7.4.0");var subQ2=sQuery(id+"F0.wireOp",EDGE,"E16.MirrorCS");var subQ3=sQuery(id+"F0.wireOp",EDGE,"E17.MirrorCS");Q5=makeQuery(id+"F5.boolean.opBoolean","SPLIT",EDGE,{"disambiguationData":[TD([makeQuery(id+"F5.opExtrude","SWEPT_FACE",FACE,{"disambiguationData":[OSD([subQ1])]})])],"derivedFrom":makeQuery(id+"F1.opRevolve","SWEPT_EDGE",EDGE,{"disambiguationData":[OSD([subQ2,subQ3])]})});}
            var Q6;
            {var subQ1=sQuery(id+"F4.wireOp",EDGE,"E36.7.3.0");var subQ2=sQuery(id+"F0.wireOp",EDGE,"E16.MirrorCS");var subQ3=sQuery(id+"F0.wireOp",EDGE,"E17.MirrorCS");Q6=makeQuery(id+"F5.boolean.opBoolean","SPLIT",EDGE,{"disambiguationData":[TD([makeQuery(id+"F5.opExtrude","SWEPT_FACE",FACE,{"disambiguationData":[OSD([subQ1])]})])],"derivedFrom":makeQuery(id+"F1.opRevolve","SWEPT_EDGE",EDGE,{"disambiguationData":[OSD([subQ2,subQ3])]})});}
            var Q7;
            {var subQ1=sQuery(id+"F0.wireOp",EDGE,"E16.MirrorCS");var subQ2=sQuery(id+"F4.wireOp",EDGE,"E35.2.2");var subQ3=sQuery(id+"F0.wireOp",EDGE,"E17.MirrorCS");Q7=makeQuery(id+"F5.boolean.opBoolean","SPLIT",EDGE,{"disambiguationData":[TD([makeQuery(id+"F5.opExtrude","SWEPT_FACE",FACE,{"disambiguationData":[OSD([subQ2])]})])],"derivedFrom":makeQuery(id+"F1.opRevolve","SWEPT_EDGE",EDGE,{"disambiguationData":[OSD([subQ1,subQ3])]})});}
            var Q8;
            {var subQ0=sQuery(id+"F0.wireOp",EDGE,"E16.MirrorCS");var subQ2=sQuery(id+"F4.wireOp",EDGE,"E35.1.2");var subQ3=sQuery(id+"F0.wireOp",EDGE,"E17.MirrorCS");Q8=makeQuery(id+"F5.boolean.opBoolean","SPLIT",EDGE,{"disambiguationData":[TD([makeQuery(id+"F5.opExtrude","SWEPT_FACE",FACE,{"disambiguationData":[OSD([subQ2])]})])],"derivedFrom":makeQuery(id+"F1.opRevolve","SWEPT_EDGE",EDGE,{"disambiguationData":[OSD([subQ0,subQ3])]})});}
            var Q9;
            {var subQ0=sQuery(id+"F0.wireOp",EDGE,"E16.MirrorCS");var subQ2=sQuery(id+"F0.wireOp",EDGE,"E17.MirrorCS");var subQ3=sQuery(id+"F4.wireOp",EDGE,"E26.0");Q9=makeQuery(id+"F5.boolean.opBoolean","SPLIT",EDGE,{"disambiguationData":[TD([makeQuery(id+"F5.opExtrude","SWEPT_FACE",FACE,{"disambiguationData":[OSD([subQ3])]})])],"derivedFrom":makeQuery(id+"F1.opRevolve","SWEPT_EDGE",EDGE,{"disambiguationData":[OSD([subQ0,subQ2])]})});}
            var Q10;
            {var subQ0=sQuery(id+"F4.wireOp",EDGE,"E25.0");var subQ1=sQuery(id+"F0.wireOp",EDGE,"E16.MirrorCS");var subQ2=sQuery(id+"F0.wireOp",EDGE,"E17.MirrorCS");Q10=makeQuery(id+"F5.boolean.opBoolean","SPLIT",EDGE,{"disambiguationData":[TD([makeQuery(id+"F5.opExtrude","SWEPT_FACE",FACE,{"disambiguationData":[OSD([subQ0])]})])],"derivedFrom":makeQuery(id+"F1.opRevolve","SWEPT_EDGE",EDGE,{"disambiguationData":[OSD([subQ1,subQ2])]})});}
            var Q11;
            {var subQ0=sQuery(id+"F0.wireOp",EDGE,"E16.MirrorCS");var subQ2=sQuery(id+"F0.wireOp",EDGE,"E17.MirrorCS");var subQ3=sQuery(id+"F4.wireOp",EDGE,"E36.7.12.0");Q11=makeQuery(id+"F5.boolean.opBoolean","SPLIT",EDGE,{"disambiguationData":[TD([makeQuery(id+"F5.opExtrude","SWEPT_FACE",FACE,{"disambiguationData":[OSD([subQ3])]})])],"derivedFrom":makeQuery(id+"F1.opRevolve","SWEPT_EDGE",EDGE,{"disambiguationData":[OSD([subQ0,subQ2])]})});}
            var Q12;
            {var subQ0=sQuery(id+"F0.wireOp",EDGE,"E16.MirrorCS");var subQ1=sQuery(id+"F0.wireOp",EDGE,"E17.MirrorCS");var subQ3=sQuery(id+"F4.wireOp",EDGE,"E36.7.11.0");Q12=makeQuery(id+"F5.boolean.opBoolean","SPLIT",EDGE,{"disambiguationData":[TD([makeQuery(id+"F5.opExtrude","SWEPT_FACE",FACE,{"disambiguationData":[OSD([subQ3])]})])],"derivedFrom":makeQuery(id+"F1.opRevolve","SWEPT_EDGE",EDGE,{"disambiguationData":[OSD([subQ0,subQ1])]})});}
            var Q13;
            {var subQ0=sQuery(id+"F0.wireOp",EDGE,"E16.MirrorCS");var subQ1=sQuery(id+"F0.wireOp",EDGE,"E17.MirrorCS");var subQ3=sQuery(id+"F4.wireOp",EDGE,"E36.7.10.0");Q13=makeQuery(id+"F5.boolean.opBoolean","SPLIT",EDGE,{"disambiguationData":[TD([makeQuery(id+"F5.opExtrude","SWEPT_FACE",FACE,{"disambiguationData":[OSD([subQ3])]})])],"derivedFrom":makeQuery(id+"F1.opRevolve","SWEPT_EDGE",EDGE,{"disambiguationData":[OSD([subQ0,subQ1])]})});}
            fillet(context, id + "F9", {"entities" : qUnion([Q0, Q1, Q2, Q3, Q4, Q5, Q6, Q7, Q8, Q9, Q10, Q11, Q12, Q13]), "radius" : 5 * mm, "tangentPropagation" : true, "allowEdgeOverflow" : false});
        }
        {
            var Q0;
            Q0=makeQuery(id+"F5.opExtrude","CAP_EDGE",EDGE,{"disambiguationData":[OSD([sQuery(id+"F4.wireOp",EDGE,"E36.5.13.0")])],"isStart":false});
            var Q1;
            Q1=makeQuery(id+"F5.opExtrude","CAP_EDGE",EDGE,{"disambiguationData":[OSD([sQuery(id+"F4.wireOp",EDGE,"E36.5.12.0")])],"isStart":false});
            var Q2;
            Q2=makeQuery(id+"F5.opExtrude","CAP_EDGE",EDGE,{"disambiguationData":[OSD([sQuery(id+"F4.wireOp",EDGE,"E24")])],"isStart":false});
            var Q3;
            Q3=makeQuery(id+"F5.opExtrude","CAP_EDGE",EDGE,{"disambiguationData":[OSD([sQuery(id+"F4.wireOp",EDGE,"E35.1.0")])],"isStart":false});
            var Q4;
            Q4=makeQuery(id+"F5.opExtrude","CAP_EDGE",EDGE,{"disambiguationData":[OSD([sQuery(id+"F4.wireOp",EDGE,"E35.2.0")])],"isStart":false});
            var Q5;
            Q5=makeQuery(id+"F5.opExtrude","CAP_EDGE",EDGE,{"disambiguationData":[OSD([sQuery(id+"F4.wireOp",EDGE,"E36.5.3.0")])],"isStart":false});
            var Q6;
            Q6=makeQuery(id+"F5.opExtrude","CAP_EDGE",EDGE,{"disambiguationData":[OSD([sQuery(id+"F4.wireOp",EDGE,"E36.5.11.0")])],"isStart":false});
            var Q7;
            Q7=makeQuery(id+"F5.opExtrude","CAP_EDGE",EDGE,{"disambiguationData":[OSD([sQuery(id+"F4.wireOp",EDGE,"E36.5.10.0")])],"isStart":false});
            var Q8;
            Q8=makeQuery(id+"F5.opExtrude","CAP_EDGE",EDGE,{"disambiguationData":[OSD([sQuery(id+"F4.wireOp",EDGE,"E36.5.4.0")])],"isStart":false});
            var Q9;
            Q9=makeQuery(id+"F5.opExtrude","CAP_EDGE",EDGE,{"disambiguationData":[OSD([sQuery(id+"F4.wireOp",EDGE,"E36.5.5.0")])],"isStart":false});
            var Q10;
            Q10=makeQuery(id+"F5.opExtrude","CAP_EDGE",EDGE,{"disambiguationData":[OSD([sQuery(id+"F4.wireOp",EDGE,"E36.5.6.0")])],"isStart":false});
            var Q11;
            Q11=makeQuery(id+"F5.opExtrude","CAP_EDGE",EDGE,{"disambiguationData":[OSD([sQuery(id+"F4.wireOp",EDGE,"E36.5.7.0")])],"isStart":false});
            var Q12;
            Q12=makeQuery(id+"F5.opExtrude","CAP_EDGE",EDGE,{"disambiguationData":[OSD([sQuery(id+"F4.wireOp",EDGE,"E36.5.8.0")])],"isStart":false});
            var Q13;
            Q13=makeQuery(id+"F5.opExtrude","CAP_EDGE",EDGE,{"disambiguationData":[OSD([sQuery(id+"F4.wireOp",EDGE,"E36.5.9.0")])],"isStart":false});
            fillet(context, id + "F10", {"entities" : qUnion([Q0, Q1, Q2, Q3, Q4, Q5, Q6, Q7, Q8, Q9, Q10, Q11, Q12, Q13]), "radius" : 3 * mm, "tangentPropagation" : true, "allowEdgeOverflow" : false});
        }
        {
            var Q0;
            Q0=makeQuery(id+"F5.opExtrude","CAP_EDGE",EDGE,{"disambiguationData":[OSD([sQuery(id+"F4.wireOp",EDGE,"E35.1.0")])],"isStart":true});
            var Q1;
            {var subQ1=sQuery(id+"F4.wireOp",EDGE,"E24");var subQ2=sQuery(id+"F4.wireOp",EDGE,"E25.0");Q1=makeQuery(id+"F7.boolean.opBoolean","SPLIT",EDGE,{"disambiguationData":[TD([makeQuery(id+"F5.opExtrude","SWEPT_FACE",FACE,{"disambiguationData":[OSD([subQ2])]})])],"derivedFrom":makeQuery(id+"F5.opExtrude","CAP_EDGE",EDGE,{"disambiguationData":[OSD([subQ1])],"isStart":true})});}
            var Q2;
            {var subQ1=sQuery(id+"F4.wireOp",EDGE,"E26.0");var subQ2=sQuery(id+"F4.wireOp",EDGE,"E24");Q2=makeQuery(id+"F7.boolean.opBoolean","SPLIT",EDGE,{"disambiguationData":[TD([makeQuery(id+"F5.opExtrude","SWEPT_FACE",FACE,{"disambiguationData":[OSD([subQ1])]})])],"derivedFrom":makeQuery(id+"F5.opExtrude","CAP_EDGE",EDGE,{"disambiguationData":[OSD([subQ2])],"isStart":true})});}
            var Q3;
            Q3=makeQuery(id+"F5.opExtrude","CAP_EDGE",EDGE,{"disambiguationData":[OSD([sQuery(id+"F4.wireOp",EDGE,"E36.5.13.0")])],"isStart":true});
            var Q4;
            Q4=makeQuery(id+"F5.opExtrude","CAP_EDGE",EDGE,{"disambiguationData":[OSD([sQuery(id+"F4.wireOp",EDGE,"E36.5.12.0")])],"isStart":true});
            var Q5;
            Q5=makeQuery(id+"F5.opExtrude","CAP_EDGE",EDGE,{"disambiguationData":[OSD([sQuery(id+"F4.wireOp",EDGE,"E36.5.11.0")])],"isStart":true});
            var Q6;
            Q6=makeQuery(id+"F5.opExtrude","CAP_EDGE",EDGE,{"disambiguationData":[OSD([sQuery(id+"F4.wireOp",EDGE,"E36.5.10.0")])],"isStart":true});
            var Q7;
            Q7=makeQuery(id+"F5.opExtrude","CAP_EDGE",EDGE,{"disambiguationData":[OSD([sQuery(id+"F4.wireOp",EDGE,"E36.5.9.0")])],"isStart":true});
            var Q8;
            Q8=makeQuery(id+"F5.opExtrude","CAP_EDGE",EDGE,{"disambiguationData":[OSD([sQuery(id+"F4.wireOp",EDGE,"E36.5.8.0")])],"isStart":true});
            var Q9;
            Q9=makeQuery(id+"F5.opExtrude","CAP_EDGE",EDGE,{"disambiguationData":[OSD([sQuery(id+"F4.wireOp",EDGE,"E36.5.7.0")])],"isStart":true});
            var Q10;
            Q10=makeQuery(id+"F5.opExtrude","CAP_EDGE",EDGE,{"disambiguationData":[OSD([sQuery(id+"F4.wireOp",EDGE,"E36.5.6.0")])],"isStart":true});
            var Q11;
            Q11=makeQuery(id+"F5.opExtrude","CAP_EDGE",EDGE,{"disambiguationData":[OSD([sQuery(id+"F4.wireOp",EDGE,"E36.5.5.0")])],"isStart":true});
            var Q12;
            Q12=makeQuery(id+"F5.opExtrude","CAP_EDGE",EDGE,{"disambiguationData":[OSD([sQuery(id+"F4.wireOp",EDGE,"E36.5.4.0")])],"isStart":true});
            var Q13;
            Q13=makeQuery(id+"F5.opExtrude","CAP_EDGE",EDGE,{"disambiguationData":[OSD([sQuery(id+"F4.wireOp",EDGE,"E36.5.3.0")])],"isStart":true});
            var Q14;
            Q14=makeQuery(id+"F5.opExtrude","CAP_EDGE",EDGE,{"disambiguationData":[OSD([sQuery(id+"F4.wireOp",EDGE,"E35.2.0")])],"isStart":true});
            fillet(context, id + "F11", {"entities" : qUnion([Q0, Q1, Q2, Q3, Q4, Q5, Q6, Q7, Q8, Q9, Q10, Q11, Q12, Q13, Q14]), "radius" : 3 * mm, "tangentPropagation" : true, "allowEdgeOverflow" : false});
        }
        {
            var Q0;
            Q0=makeQuery(id+"F1.opRevolve","SWEPT_EDGE",EDGE,{"disambiguationData":[OSD([sQuery(id+"F0.wireOp",EDGE,"E4"),sQuery(id+"F0.wireOp",EDGE,"E5")])]});
            fillet(context, id + "F12", {"entities" : qUnion([Q0]), "radius" : 5 * mm, "tangentPropagation" : true, "allowEdgeOverflow" : false});
        }
        {
            var Q0;
            Q0=makeQuery(id+"F1.opRevolve","SWEPT_EDGE",EDGE,{"disambiguationData":[OSD([sQuery(id+"F0.wireOp",EDGE,"E13.MirrorCS"),sQuery(id+"F0.wireOp",EDGE,"E14.MirrorCS")])]});
            fillet(context, id + "F13", {"entities" : qUnion([Q0]), "radius" : 5 * mm, "tangentPropagation" : true, "allowEdgeOverflow" : false});
        }
        {
            var Q0;
            Q0=makeQuery(id+"F1.opRevolve","SWEPT_FACE",FACE,{"disambiguationData":[OSD([sQuery(id+"F0.wireOp",EDGE,"E10.MirrorCS")])]});
            fillet(context, id + "F14", {"entities" : qUnion([Q0]), "radius" : 5 * mm, "tangentPropagation" : true, "allowEdgeOverflow" : false});
        }
        {
            var Q0;
            Q0=makeQuery(id+"F1.opRevolve","SWEPT_EDGE",EDGE,{"disambiguationData":[OSD([sQuery(id+"F0.wireOp",EDGE,"E1"),sQuery(id+"F0.wireOp",EDGE,"E2")])]});
            fillet(context, id + "F15", {"entities" : qUnion([Q0]), "radius" : 5 * mm, "tangentPropagation" : true, "allowEdgeOverflow" : false});
        }
    });
